# Revit family: 0048018 Sylvania Lighting Fixture SYLVEO RGBW IP66
name_source: partatom
category: Lighting Fixtures
revit_build: Autodesk Revit 2016 (Build: 20150220_1215(x64)
units: mm (PartAtom-declared; Revit-internal decimal feet)

## family parameters
Cut with Voids When Loaded = No
Host = Face
Light Source = No
OmniClass Number = 23.80.70.00
OmniClass Title = Lighting
Part Type = Normal
Room Calculation Point = No
Round Connector Dimension = Use Diameter
Shared = No

## types (1)
- 0048018 SYLVEO RGBW IP66 170W ASYM SIL
    100W_SYL = No
    30/50W_SYL = No
    Apparent Load = 170 VA
    Assembly Code = D5020200
    AssetType = Fixed
    AxisHeightBracket_SYL = 110 mm  [stored 0.360892 ft]
    ChamferBracket_SYL = 22 mm  [stored 0.0721785 ft]
    ClassificationName = Uniclass2015
    ClassificationValue = EF_70_80
    Cost = 0 $
    Default Elevation = 1219 mm
    DepthBracket_SYL = 48 mm  [stored 0.15748 ft]
    DiameterCylinder_SYL = 63 mm  [stored 0.206693 ft]
    DocumentationLiterature = http://www.sylvania-lighting.com
    DurationUnit = hours
    ElectricShockClassification = Class I
    ExpectedLife = 50000
    IfcExportAs = IfcLightFixtureType
    IfcExportType = IfcLightFixtureType
    ImpactProtectionIndex = IK08
    IngressProtection = IP66
    InputNominalFrequency = 50/60 Hz
    InputVoltage = 100-240V~
    Keynote = 16500
    Lamp = LED
    LampsType = LED
    LuminousEfficacy = 48.750 lm/W
    Manufacturer = Feilo Sylvania
    ManufacturerName = Feilo Sylvania
    Material_1_SYL = Body-Sylvania-Sylveo-RAL9006
    Model = Sylveo RGBW IP66 170W ASYM SIL
    ModelNumber = 0048018
    ModelReference = Sylveo RGBW IP66 170W ASYM SIL
    Name = Sylveo RGBW IP66 170W ASYM SIL
    NominalDepth = 0 mm  [stored 0 ft]
    NominalHeight = 0 mm  [stored 0 ft]
    NominalLength = 0 mm  [stored 0 ft]
    PowerFactor = 0
    ThicknessBracket_SYL = 4 mm  [stored 0.0131234 ft]
    Type Image = <None>
    TypeName = Sylveo RGBW IP66 170W ASYM SIL
    URL = http://www.sylvania-lighting.com
    Voltage = 0 V
    Weight = 13.5 kg
    WidthBracketIn_SYL = 434 mm  [stored 1.42388 ft]
    WidthCylinder_SYL = 15 mm  [stored 0.0492126 ft]

note: [stored X ft] marks values corroborated as IEEE doubles in the binary element streams (Revit-internal decimal feet)

## geometry (parser evidence)
native form markers: Sweep x3
no freeform markers — native parametric forms only
